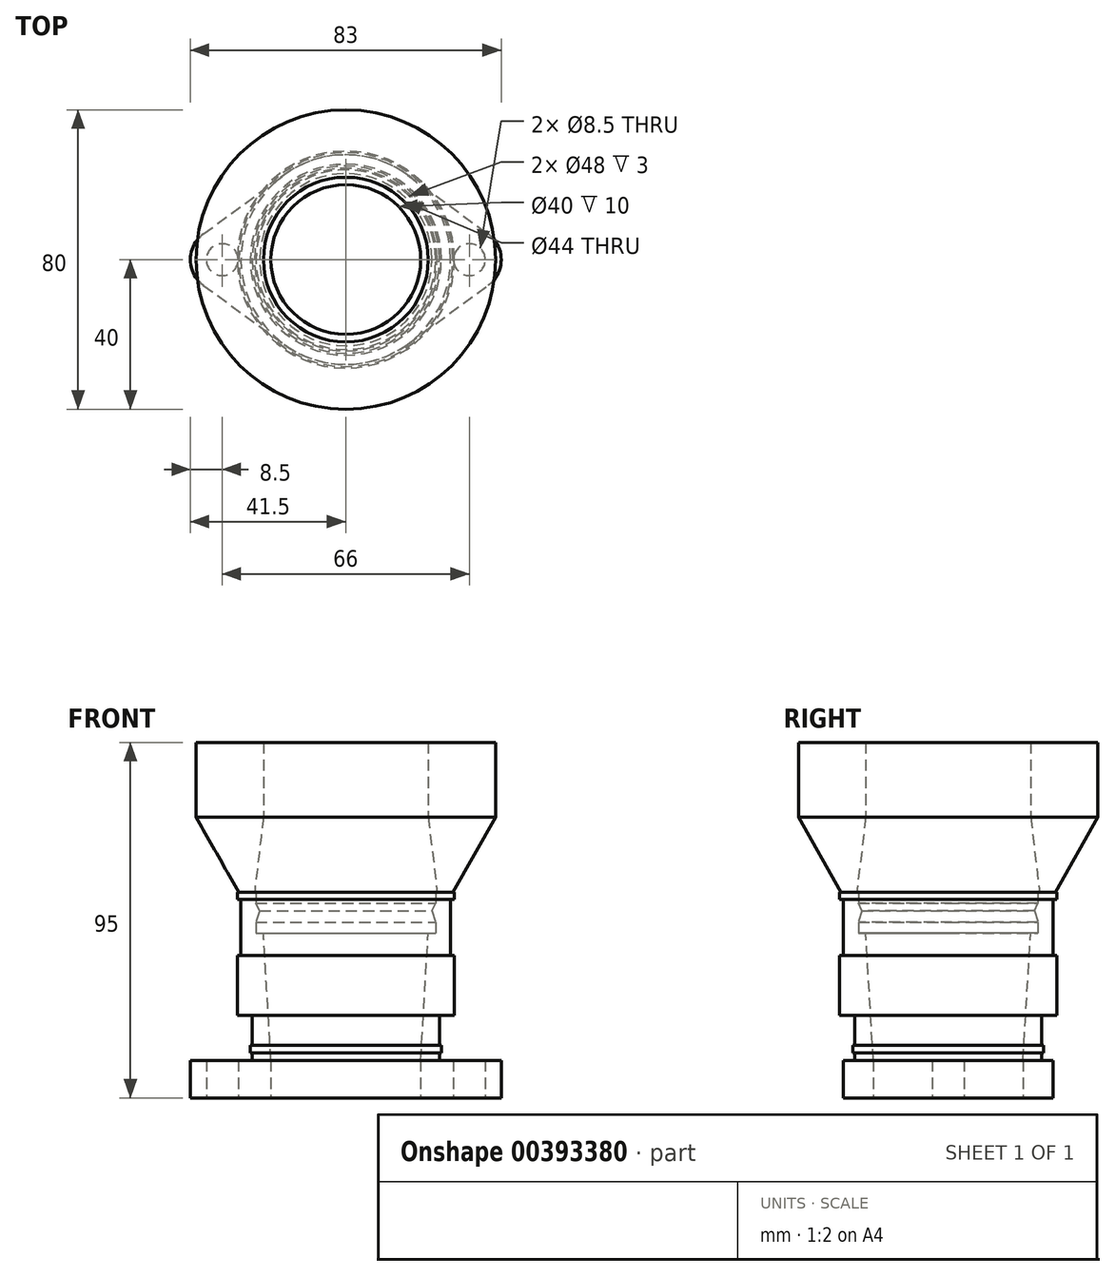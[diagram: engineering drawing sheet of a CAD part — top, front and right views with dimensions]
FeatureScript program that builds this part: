
annotation { "Feature Type Name" : "Feature", "Feature Type Description" : "" }
export const myFeature = defineFeature(function(context is Context, id is Id, definition is map)
    precondition{}
    {
        {
            var Q0;
            Q0=qCreatedBy(makeId("Top.planeOp"),FACE);
            var sketch = newSketch(context, id + "F0", { "sketchPlane" : qUnion([Q0])});
            skCircle(sketch, "E0", {"center": v(0, 0) * mm, "radius": 20 * mm});
            skCircle(sketch, "E1", {"center": v(-33, 0) * mm, "radius": 4.25 * mm});
            skCircle(sketch, "E2", {"center": v(33, 0) * mm, "radius": 4.25 * mm});
            skArc(sketch, "E3", {"start": v(-38.02, 6.86) * mm, "mid": v(-41.5, 0) * mm, "end": v(-38.02, -6.86) * mm});
            skArc(sketch, "E4", {"start": v(16.55, 22.59) * mm, "mid": v(0, 28) * mm, "end": v(-16.55, 22.59) * mm});
            skArc(sketch, "E5", {"start": v(38.02, -6.86) * mm, "mid": v(41.5, 0) * mm, "end": v(38.02, 6.86) * mm});
            skLineSegment(sketch, "E6", {"start": v(-38.02, 6.86) * mm, "end": v(-16.55, 22.59) * mm});
            skLineSegment(sketch, "E7", {"start": v(-38.02, -6.86) * mm, "end": v(-16.55, -22.59) * mm});
            skLineSegment(sketch, "E8", {"start": v(16.55, 22.59) * mm, "end": v(38.02, 6.86) * mm});
            skLineSegment(sketch, "E9", {"start": v(16.55, -22.59) * mm, "end": v(38.02, -6.86) * mm});
            skPoint(sketch, "E10.orphan", {"position": v(7.33, -40.07) * mm});
            skPoint(sketch, "E11.orphan", {"position": v(7.33, 40.07) * mm});
            skArc(sketch, "E12.trimOffspring", {"start": v(-16.55, -22.59) * mm, "mid": v(0, -28) * mm, "end": v(16.55, -22.59) * mm});
            skSolve(sketch);
        }
        {
            var Q0;
            Q0 = qSketchRegion(id + "F0", true);
            extrude(context, id + "F1", {"entities" : qUnion([Q0]), "depth" : 10 * mm});
        }
        {
            var Q0;
            Q0=qCreatedBy(makeId("Front.planeOp"),FACE);
            var sketch = newSketch(context, id + "F2", { "sketchPlane" : qUnion([Q0])});
            skLineSegment(sketch, "E13", {"start": v(22, 44) * mm, "end": v(24, 44) * mm});
            skLineSegment(sketch, "E14", {"start": v(24, 44) * mm, "end": v(24, 47) * mm});
            skLineSegment(sketch, "E15", {"start": v(24, 47) * mm, "end": v(23, 50) * mm});
            skLineSegment(sketch, "E16", {"start": v(23, 50) * mm, "end": v(24, 52) * mm});
            skLineSegment(sketch, "E17", {"start": v(24, 52) * mm, "end": v(24, 55) * mm});
            skLineSegment(sketch, "E18", {"start": v(24, 55) * mm, "end": v(29, 55) * mm});
            skLineSegment(sketch, "E19", {"start": v(25, 10) * mm, "end": v(20, 10) * mm});
            skLineSegment(sketch, "E20", {"start": v(0, 0) * mm, "end": v(0, 54.76) * mm, "construction": true});
            skLineSegment(sketch, "E21", {"start": v(22, 44) * mm, "end": v(20, 10) * mm});
            skLineSegment(sketch, "E22", {"start": v(29, 55) * mm, "end": v(29, 53) * mm});
            skLineSegment(sketch, "E23", {"start": v(29, 53) * mm, "end": v(28, 53) * mm});
            skLineSegment(sketch, "E24", {"start": v(28, 53) * mm, "end": v(28, 38) * mm});
            skLineSegment(sketch, "E25", {"start": v(28, 38) * mm, "end": v(29, 38) * mm});
            skLineSegment(sketch, "E26", {"start": v(29, 38) * mm, "end": v(29, 22) * mm});
            skLineSegment(sketch, "E27", {"start": v(25, 10) * mm, "end": v(25, 12) * mm});
            skLineSegment(sketch, "E28", {"start": v(25, 22) * mm, "end": v(29, 22) * mm});
            skLineSegment(sketch, "E29", {"start": v(25, 12) * mm, "end": v(25.5, 12) * mm});
            skLineSegment(sketch, "E30", {"start": v(25.5, 12) * mm, "end": v(25.5, 14) * mm});
            skLineSegment(sketch, "E31", {"start": v(25.5, 14) * mm, "end": v(25, 14) * mm});
            skLineSegment(sketch, "E32.trimOffspring", {"start": v(25, 14) * mm, "end": v(25, 22) * mm});
            skSolve(sketch);
        }
        {
            var Q0;
            Q0 = qSketchRegion(id + "F2", true);
            var Q1;
            Q1=sQuery(id+"F2.wireOp",EDGE,"E20");
            revolve(context, id + "F3", {"operationType" : NewBodyOperationType.ADD, "entities" : qUnion([Q0]), "axis" : qUnion([Q1]), "revolveType" : RevolveType.FULL});
        }
        {
            var Q0;
            Q0=qCreatedBy(makeId("Front.planeOp"),FACE);
            var sketch = newSketch(context, id + "F4", { "sketchPlane" : qUnion([Q0])});
            skLineSegment(sketch, "E33", {"start": v(-24.4, 55) * mm, "end": v(-22, 75) * mm});
            skLineSegment(sketch, "E34", {"start": v(-40, 75) * mm, "end": v(-28.6, 55) * mm});
            skLineSegment(sketch, "E35", {"start": v(0, 0) * mm, "end": v(0, 93.18) * mm, "construction": true});
            skLineSegment(sketch, "E36", {"start": v(-28.6, 55) * mm, "end": v(-24.4, 55) * mm});
            skLineSegment(sketch, "E37", {"start": v(-40, 75) * mm, "end": v(-40, 95) * mm});
            skLineSegment(sketch, "E38", {"start": v(-40, 95) * mm, "end": v(-22, 95) * mm});
            skLineSegment(sketch, "E39", {"start": v(-22, 95) * mm, "end": v(-22, 75) * mm});
            skSolve(sketch);
        }
        {
            var Q0;
            Q0 = qSketchRegion(id + "F4", true);
            var Q1;
            Q1=sQuery(id+"F4.wireOp",EDGE,"E35");
            revolve(context, id + "F5", {"operationType" : NewBodyOperationType.ADD, "entities" : qUnion([Q0]), "axis" : qUnion([Q1]), "revolveType" : RevolveType.FULL});
        }
    });
